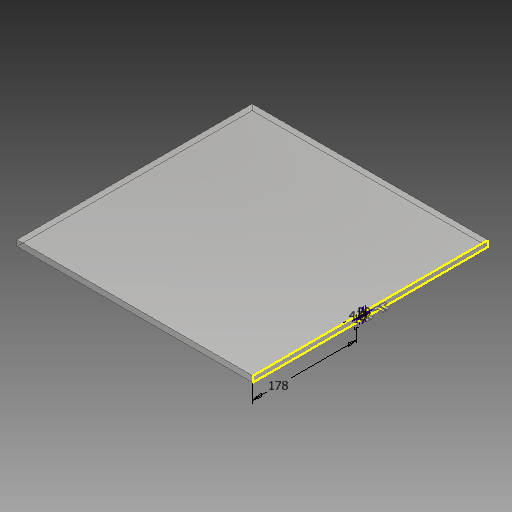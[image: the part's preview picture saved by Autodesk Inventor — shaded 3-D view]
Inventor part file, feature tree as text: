
AUTODESK INVENTOR PART (.ipt)
format: ipt  version: 2018.3 (Build 223284000, 284)  size: 161,280 bytes
history: native  units: mm
features: extrude x3, sketch x2, pattern_linear x1, projected_geometry x1
ambient origin geometry x8: Origin, YZ Plane, XZ Plane, XY Plane, X Axis, Y Axis, Z Axis, Center Point
bodies: Volumenkörper1 (feature_tree)
feature tree (7):
  extrude  "Extrusion1"  Depth=400.0mm
  sketch  "Skizze2"  dims[d2=10.0mm d3=0.0mm d4=20.0mm d5=1.0mm d6=11.0mm d7=2.0mm d8=4.5mm d10=178.0mm d11=4.0mm d12=0.0mm d15=13.0mm d16=0.0mm d17=20.0mm d19=27.0mm]
  extrude  "Extrusion2"  Depth=20.0mm
  extrude  "Extrusion4"  Depth=1.0mm
  pattern_linear  "Rechteckige Anordnung1"  Spacing1=11.0mm  [1 undecoded]
  sketch  "Skizze1"  dims[d0=400.0mm d1=400.0mm]
  projected_geometry  "Projizierte Kontur1"
note: 1 required parameter value undecoded (feature->parameter linkage not recoverable at this tier; creation-order binding heuristic only, values carry confidence <= 0.55)
